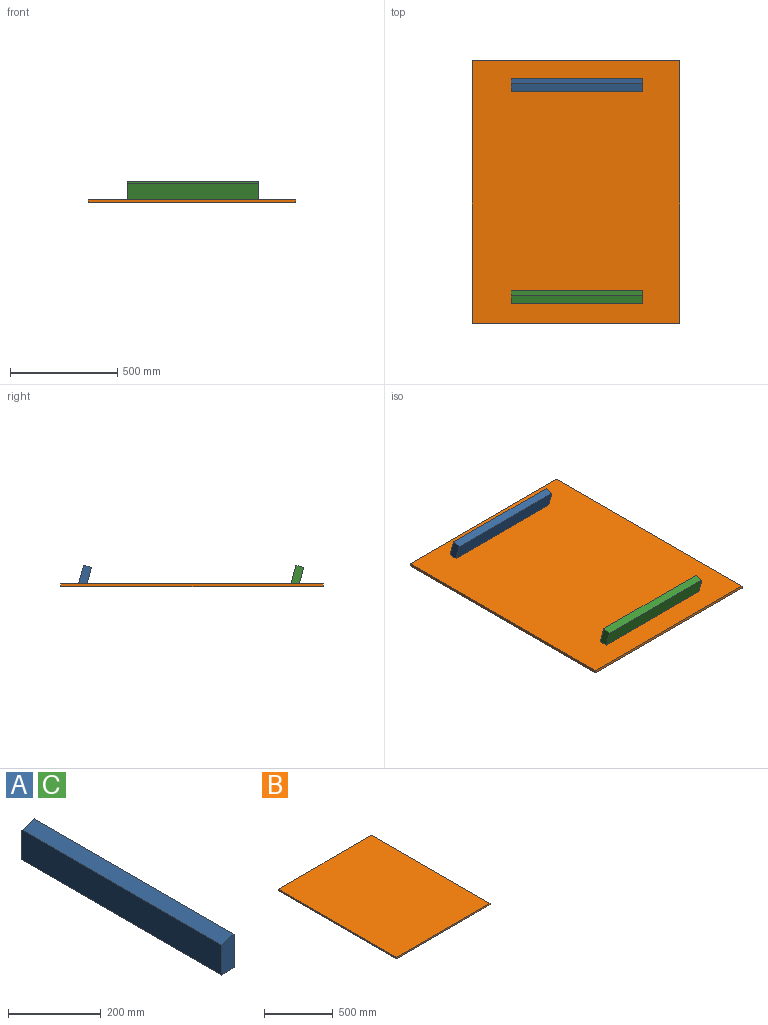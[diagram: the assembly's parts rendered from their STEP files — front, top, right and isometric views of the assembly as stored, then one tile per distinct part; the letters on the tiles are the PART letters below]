
ASSEMBLY  parts=3 mates=3
PART A: 6 faces, bbox 38.1x609.6x89.2 mm
  f0: plane 609.6x38.1mm, normal (0.01,0,-1), area 23225.8mm2, adj f1,f3,f4,f5
  f1: plane 609.6x88.9mm, normal (1,0,0), area 54193.4mm2, adj f0,f2,f4,f5
  f2: plane 609.6x38.1mm, normal (-0.26,0,0.97), area 24044.8mm2, adj f1,f3,f4,f5
  f3: plane 609.6x78.96mm, normal (-1,0,0), area 48136.6mm2, adj f0,f2,f4,f5
  f4: plane 89.18x38.1mm, normal (0,-1,0), area 3197.7mm2, adj f0,f1,f2,f3
  f5: plane 89.18x38.1mm, normal (0,1,0), area 3197.7mm2, adj f0,f1,f2,f3
PART B: 6 faces, bbox 965.2x1219.2x12.7 mm
  f0: plane 965.2x12.7mm, normal (0,-1,0), area 12258mm2, adj f1,f3,f4,f5
  f1: plane 1219.2x12.7mm, normal (1,0,0), area 15483.8mm2, adj f0,f2,f4,f5
  f2: plane 965.2x12.7mm, normal (0,1,0), area 12258mm2, adj f1,f3,f4,f5
  f3: plane 1219.2x12.7mm, normal (-1,0,0), area 15483.8mm2, adj f0,f2,f4,f5
  f4: plane 1219.2x965.2mm, normal (0,0,1), area 1176771.8mm2, adj f0,f1,f2,f3
  f5: plane 1219.2x965.2mm, normal (0,0,-1), area 1176771.8mm2, adj f0,f1,f2,f3
PART C: same geometry as A
PLACE A rot(axis=(-0.7,-0.7,-0.09),169.4deg) t=(308.82,497.66,50.7)mm
PLACE B at identity fixed
PLACE C rot(axis=(-0.7,-0.7,-0.09),169.4deg) t=(308.82,-490.05,50.7)mm
MATE planar A.f4 <-> C.f4  axis (-1,0,0) through (-300.78,497.36,53.28)mm
MATE planar A.f2 <-> B.f4  axis (0,0,-1) through (4.02,507.85,12.7)mm
MATE planar C.f2 <-> B.f4  axis (0,0,-1) through (4.02,-479.86,12.7)mm
